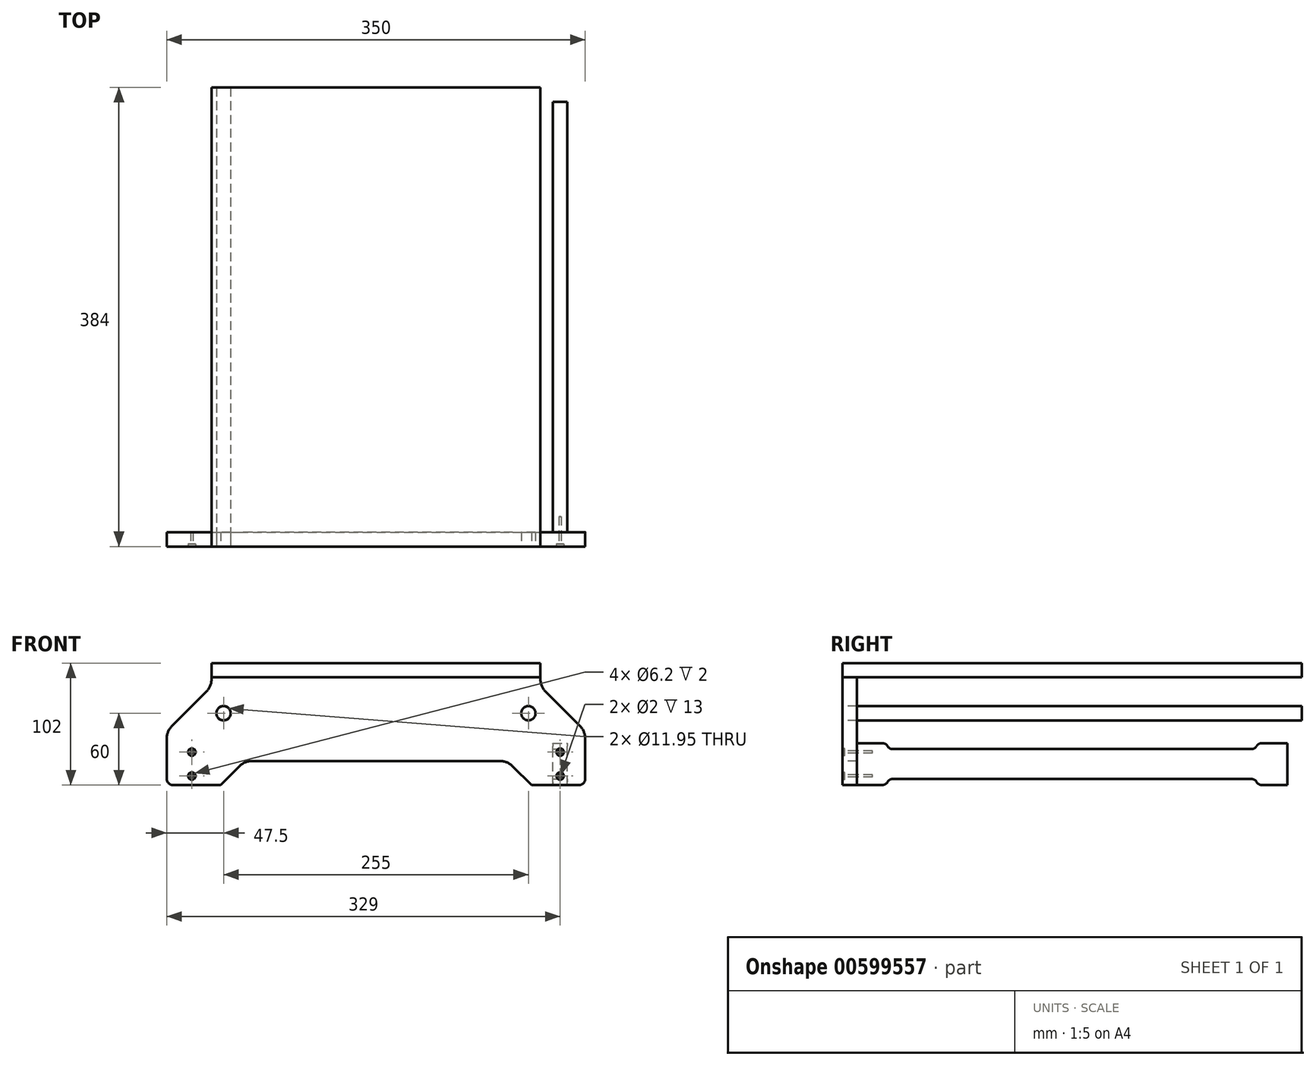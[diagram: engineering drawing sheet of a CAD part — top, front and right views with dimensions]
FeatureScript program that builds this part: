
annotation { "Feature Type Name" : "Feature", "Feature Type Description" : "" }
export const myFeature = defineFeature(function(context is Context, id is Id, definition is map)
    precondition{}
    {
        {
            var Q0;
            Q0=qCreatedBy(makeId("Front.planeOp"),FACE);
            var sketch = newSketch(context, id + "F0", { "sketchPlane" : qUnion([Q0])});
            skLineSegment(sketch, "E0.bottom", {"start": v(-137.5, 0) * mm, "end": v(137.5, 0) * mm});
            skLineSegment(sketch, "E0.top", {"start": v(-175, -90) * mm, "end": v(175, -90) * mm});
            skLineSegment(sketch, "E0.left", {"start": v(-137.5, 0) * mm, "end": v(-175, -90) * mm, "construction": true});
            skLineSegment(sketch, "E0.right", {"start": v(137.5, 0) * mm, "end": v(175, -90) * mm, "construction": true});
            skLineSegment(sketch, "E1", {"start": v(0, 0) * mm, "end": v(0, -90) * mm, "construction": true});
            skLineSegment(sketch, "E2", {"start": v(-175, -90) * mm, "end": v(-175, -45) * mm});
            skLineSegment(sketch, "E3", {"start": v(-175, -45) * mm, "end": v(-137.5, -7.5) * mm});
            skLineSegment(sketch, "E4", {"start": v(-137.5, -7.5) * mm, "end": v(-137.5, 0) * mm});
            skLineSegment(sketch, "E5.MirrorCS", {"start": v(137.5, -7.5) * mm, "end": v(137.5, 0) * mm});
            skLineSegment(sketch, "E6.MirrorCS", {"start": v(175, -45) * mm, "end": v(137.5, -7.5) * mm});
            skLineSegment(sketch, "E7.MirrorCS", {"start": v(175, -90) * mm, "end": v(175, -45) * mm});
            skSolve(sketch);
        }
        {
            var Q0;
            Q0 = qSketchRegion(id + "F0", true);
            extrude(context, id + "F1", {"entities" : qUnion([Q0]), "depth" : 12 * mm, "offsetDistance" : 25 * mm});
        }
        {
            var Q0;
            Q0=makeQuery(id+"F1.opExtrude","CAP_FACE",FACE,{"disambiguationData":[OSD([sQuery(id+"F0.wireOp",EDGE,"E0.bottom"),sQuery(id+"F0.wireOp",EDGE,"E0.top"),sQuery(id+"F0.wireOp",EDGE,"Db9297z0-HztM-tPDV-7j2n-pV0MaHttiBtU"),sQuery(id+"F0.wireOp",EDGE,"ws5DMRmw-QTd8-vzda-Jt7f-uyXxEBe4kZxb"),sQuery(id+"F0.wireOp",EDGE,"MvMPfKiF-jqBY-hYbT-wa1q-WH4llltNyERM"),sQuery(id+"F0.wireOp",EDGE,"yXXL3qDJ-5hGa-htpM-Qtsq-Fe0N1Uz4Vlwm"),sQuery(id+"F0.wireOp",EDGE,"d8d93aa3-85c5-4bdc-b8fc-1645710442690.MirrorCS"),sQuery(id+"F0.wireOp",EDGE,"6c627fb7-9931-441f-9924-80b87e4fa14c0.MirrorCS"),sQuery(id+"F0.wireOp",EDGE,"8b008a98-4391-4453-9b4b-d140ab52eb620.MirrorCS"),sQuery(id+"F0.wireOp",EDGE,"a82d0274-8465-4c41-8a39-7271eadcd95d0.MirrorCS")])],"isStart":false});
            var sketch = newSketch(context, id + "F2", { "sketchPlane" : qUnion([Q0])});
            skCircle(sketch, "E8", {"center": v(-127.5, -30) * mm, "radius": 5.97 * mm});
            skLineSegment(sketch, "E9", {"start": v(0, 0) * mm, "end": v(0, -90) * mm, "construction": true});
            skCircle(sketch, "E10.MirrorC", {"center": v(127.5, -30) * mm, "radius": 5.97 * mm});
            skLineSegment(sketch, "E11", {"start": v(-110, -70) * mm, "end": v(0, -70) * mm});
            skLineSegment(sketch, "E12", {"start": v(-130, -90) * mm, "end": v(0, -90) * mm});
            skLineSegment(sketch, "E13.MirrorCS", {"start": v(110, -70) * mm, "end": v(0, -70) * mm});
            skLineSegment(sketch, "E14.MirrorCS", {"start": v(130, -90) * mm, "end": v(0, -90) * mm});
            skLineSegment(sketch, "E15", {"start": v(-130, -90) * mm, "end": v(-110, -70) * mm});
            skLineSegment(sketch, "E16", {"start": v(110, -70) * mm, "end": v(130, -90) * mm});
            skSolve(sketch);
        }
        {
            var Q0;
            Q0 = qSketchRegion(id + "F2", true);
            extrude(context, id + "F3", {"entities" : qUnion([Q0]), "operationType" : NewBodyOperationType.REMOVE, "oppositeDirection" : true, "depth" : 25 * mm, "offsetDistance" : 25 * mm});
        }
        {
            var Q0;
            Q0=makeQuery(id+"F1.opExtrude","CAP_FACE",FACE,{"disambiguationData":[OSD([sQuery(id+"F0.wireOp",EDGE,"E0.bottom"),sQuery(id+"F0.wireOp",EDGE,"E0.top"),sQuery(id+"F0.wireOp",EDGE,"Db9297z0-HztM-tPDV-7j2n-pV0MaHttiBtU"),sQuery(id+"F0.wireOp",EDGE,"ws5DMRmw-QTd8-vzda-Jt7f-uyXxEBe4kZxb"),sQuery(id+"F0.wireOp",EDGE,"MvMPfKiF-jqBY-hYbT-wa1q-WH4llltNyERM"),sQuery(id+"F0.wireOp",EDGE,"yXXL3qDJ-5hGa-htpM-Qtsq-Fe0N1Uz4Vlwm"),sQuery(id+"F0.wireOp",EDGE,"d8d93aa3-85c5-4bdc-b8fc-1645710442690.MirrorCS"),sQuery(id+"F0.wireOp",EDGE,"6c627fb7-9931-441f-9924-80b87e4fa14c0.MirrorCS"),sQuery(id+"F0.wireOp",EDGE,"8b008a98-4391-4453-9b4b-d140ab52eb620.MirrorCS"),sQuery(id+"F0.wireOp",EDGE,"a82d0274-8465-4c41-8a39-7271eadcd95d0.MirrorCS")])],"isStart":false});
            var sketch = newSketch(context, id + "F4", { "sketchPlane" : qUnion([Q0])});
            skCircle(sketch, "E17", {"center": v(-127.5, -30) * mm, "radius": 6 * mm});
            skSolve(sketch);
        }
        {
            var Q0;
            Q0 = qSketchRegion(id + "F4", true);
            extrude(context, id + "F5", {"entities" : qUnion([Q0]), "oppositeDirection" : true, "depth" : 384 * mm, "offsetDistance" : 25 * mm});
        }
        {
            var Q0;
            Q0=makeQuery(id+"F1.opExtrude","SWEPT_FACE",FACE,{"disambiguationData":[OSD([sQuery(id+"F0.wireOp",EDGE,"E0.bottom")])]});
            var sketch = newSketch(context, id + "F6", { "sketchPlane" : qUnion([Q0])});
            skLineSegment(sketch, "E18.bottom", {"start": v(-137.5, -12) * mm, "end": v(137.5, -12) * mm});
            skLineSegment(sketch, "E18.top", {"start": v(-137.5, 372) * mm, "end": v(137.5, 372) * mm});
            skLineSegment(sketch, "E18.left", {"start": v(-137.5, -12) * mm, "end": v(-137.5, 372) * mm});
            skLineSegment(sketch, "E18.right", {"start": v(137.5, -12) * mm, "end": v(137.5, 372) * mm});
            skSolve(sketch);
        }
        {
            var Q0;
            Q0 = qSketchRegion(id + "F6", true);
            extrude(context, id + "F7", {"entities" : qUnion([Q0]), "depth" : 12 * mm, "offsetDistance" : 25 * mm});
        }
        {
            var Q0;
            Q0=makeQuery(id+"F1.opExtrude","SWEPT_EDGE",EDGE,{"disambiguationData":[OSD([sQuery(id+"F0.wireOp",EDGE,"E0.top"),sQuery(id+"F0.wireOp",EDGE,"FPoq9T64-5Oud-LrSo-KSuJ-r5LH1fMiyHHU")])]});
            var Q1;
            Q1=makeQuery(id+"F3.boolean.opBoolean","COPY",EDGE,{"derivedFrom":makeQuery(id+"F3.opExtrude","SWEPT_EDGE",EDGE,{"disambiguationData":[OSD([sQuery(id+"F0.wireOp",EDGE,"E0.top"),sQuery(id+"F2.wireOp",EDGE,"rhjKnKnN-fBDo-vWaE-Pvd1-9VDqSsNhjCKd"),sQuery(id+"F2.wireOp",EDGE,"E12")])]})});
            var Q2;
            Q2=makeQuery(id+"F3.boolean.opBoolean","COPY",EDGE,{"derivedFrom":makeQuery(id+"F3.opExtrude","SWEPT_EDGE",EDGE,{"disambiguationData":[OSD([sQuery(id+"F0.wireOp",EDGE,"E0.top"),sQuery(id+"F2.wireOp",EDGE,"dd832bca-97e2-4c86-bc4b-3068f898e1980.MirrorCS"),sQuery(id+"F2.wireOp",EDGE,"E14.MirrorCS")])]})});
            var Q3;
            Q3=makeQuery(id+"F1.opExtrude","SWEPT_EDGE",EDGE,{"disambiguationData":[OSD([sQuery(id+"F0.wireOp",EDGE,"E0.top"),sQuery(id+"F0.wireOp",EDGE,"d44177ea-6d28-4c1c-8cf6-3188f45d4e0c0.MirrorCS")])]});
            fillet(context, id + "F8", {"entities" : qUnion([Q0, Q1, Q2, Q3]), "radius" : 5 * mm, "tangentPropagation" : true, "allowEdgeOverflow" : false});
        }
        {
            var Q0;
            Q0=makeQuery(id+"F1.opExtrude","SWEPT_EDGE",EDGE,{"disambiguationData":[OSD([sQuery(id+"F0.wireOp",EDGE,"E3"),sQuery(id+"F0.wireOp",EDGE,"E4")])]});
            var Q1;
            Q1=makeQuery(id+"F1.opExtrude","SWEPT_EDGE",EDGE,{"disambiguationData":[OSD([sQuery(id+"F0.wireOp",EDGE,"E2"),sQuery(id+"F0.wireOp",EDGE,"E3")])]});
            var Q2;
            Q2=makeQuery(id+"F1.opExtrude","SWEPT_EDGE",EDGE,{"disambiguationData":[OSD([sQuery(id+"F0.wireOp",EDGE,"E5.MirrorCS"),sQuery(id+"F0.wireOp",EDGE,"E6.MirrorCS")])]});
            var Q3;
            Q3=makeQuery(id+"F1.opExtrude","SWEPT_EDGE",EDGE,{"disambiguationData":[OSD([sQuery(id+"F0.wireOp",EDGE,"E6.MirrorCS"),sQuery(id+"F0.wireOp",EDGE,"E7.MirrorCS")])]});
            var Q4;
            Q4=makeQuery(id+"F3.boolean.opBoolean","COPY",EDGE,{"derivedFrom":makeQuery(id+"F3.opExtrude","SWEPT_EDGE",EDGE,{"disambiguationData":[OSD([sQuery(id+"F2.wireOp",EDGE,"E11"),sQuery(id+"F2.wireOp",EDGE,"E15")])]})});
            var Q5;
            Q5=makeQuery(id+"F3.boolean.opBoolean","COPY",EDGE,{"derivedFrom":makeQuery(id+"F3.opExtrude","SWEPT_EDGE",EDGE,{"disambiguationData":[OSD([sQuery(id+"F2.wireOp",EDGE,"E13.MirrorCS"),sQuery(id+"F2.wireOp",EDGE,"E16")])]})});
            fillet(context, id + "F9", {"entities" : qUnion([Q0, Q1, Q2, Q3, Q4, Q5]), "radius" : 15 * mm, "tangentPropagation" : true, "allowEdgeOverflow" : false});
        }
        {
            var Q0;
            Q0=makeQuery(id+"F1.opExtrude","CAP_FACE",FACE,{"disambiguationData":[OSD([sQuery(id+"F0.wireOp",EDGE,"E0.bottom"),sQuery(id+"F0.wireOp",EDGE,"E0.top"),sQuery(id+"F0.wireOp",EDGE,"E2"),sQuery(id+"F0.wireOp",EDGE,"E3"),sQuery(id+"F0.wireOp",EDGE,"E4"),sQuery(id+"F0.wireOp",EDGE,"E5.MirrorCS"),sQuery(id+"F0.wireOp",EDGE,"E6.MirrorCS"),sQuery(id+"F0.wireOp",EDGE,"E7.MirrorCS")])],"isStart":true});
            var sketch = newSketch(context, id + "F10", { "sketchPlane" : qUnion([Q0])});
            skLineSegment(sketch, "E19.bottom", {"start": v(-148, -90) * mm, "end": v(-160, -90) * mm});
            skLineSegment(sketch, "E19.top", {"start": v(-148, -55) * mm, "end": v(-160, -55) * mm});
            skLineSegment(sketch, "E19.left", {"start": v(-148, -90) * mm, "end": v(-148, -55) * mm});
            skLineSegment(sketch, "E19.right", {"start": v(-160, -90) * mm, "end": v(-160, -55) * mm});
            skSolve(sketch);
        }
        {
            var Q0;
            Q0 = qSketchRegion(id + "F10", true);
            extrude(context, id + "F11", {"entities" : qUnion([Q0]), "depth" : 360 * mm, "offsetDistance" : 25 * mm});
        }
        {
            var Q0;
            Q0=makeQuery(id+"F1.opExtrude","CAP_FACE",FACE,{"disambiguationData":[OSD([sQuery(id+"F0.wireOp",EDGE,"E0.bottom"),sQuery(id+"F0.wireOp",EDGE,"E0.top"),sQuery(id+"F0.wireOp",EDGE,"E2"),sQuery(id+"F0.wireOp",EDGE,"E3"),sQuery(id+"F0.wireOp",EDGE,"E4"),sQuery(id+"F0.wireOp",EDGE,"E5.MirrorCS"),sQuery(id+"F0.wireOp",EDGE,"E6.MirrorCS"),sQuery(id+"F0.wireOp",EDGE,"E7.MirrorCS")])],"isStart":false});
            var sketch = newSketch(context, id + "F12", { "sketchPlane" : qUnion([Q0])});
            skCircle(sketch, "E20", {"center": v(154, -82.5) * mm, "radius": 1 * mm});
            skCircle(sketch, "E21", {"center": v(154, -62.5) * mm, "radius": 1 * mm});
            skLineSegment(sketch, "E22", {"start": v(154, -62.5) * mm, "end": v(154, -82.5) * mm, "construction": true});
            skCircle(sketch, "E23.MirrorC", {"center": v(-154, -82.5) * mm, "radius": 1 * mm});
            skCircle(sketch, "E24.MirrorC", {"center": v(-154, -62.5) * mm, "radius": 1 * mm});
            skSolve(sketch);
        }
        {
            var Q0;
            Q0 = qSketchRegion(id + "F12", true);
            extrude(context, id + "F13", {"entities" : qUnion([Q0]), "operationType" : NewBodyOperationType.REMOVE, "oppositeDirection" : true, "depth" : 25 * mm, "offsetDistance" : 25 * mm});
        }
        {
            var Q0;
            Q0=makeQuery(id+"F1.opExtrude","CAP_FACE",FACE,{"disambiguationData":[OSD([sQuery(id+"F0.wireOp",EDGE,"E0.bottom"),sQuery(id+"F0.wireOp",EDGE,"E0.top"),sQuery(id+"F0.wireOp",EDGE,"E2"),sQuery(id+"F0.wireOp",EDGE,"E3"),sQuery(id+"F0.wireOp",EDGE,"E4"),sQuery(id+"F0.wireOp",EDGE,"E5.MirrorCS"),sQuery(id+"F0.wireOp",EDGE,"E6.MirrorCS"),sQuery(id+"F0.wireOp",EDGE,"E7.MirrorCS")])],"isStart":false});
            var sketch = newSketch(context, id + "F14", { "sketchPlane" : qUnion([Q0])});
            skCircle(sketch, "E25", {"center": v(154, -62.5) * mm, "radius": 3.1 * mm});
            skCircle(sketch, "E26", {"center": v(154, -82.5) * mm, "radius": 3.1 * mm});
            skCircle(sketch, "E27", {"center": v(-154, -62.5) * mm, "radius": 3.1 * mm});
            skCircle(sketch, "E28", {"center": v(-154, -82.5) * mm, "radius": 3.1 * mm});
            skSolve(sketch);
        }
        {
            var Q0;
            Q0 = qSketchRegion(id + "F14", true);
            extrude(context, id + "F15", {"entities" : qUnion([Q0]), "operationType" : NewBodyOperationType.REMOVE, "oppositeDirection" : true, "depth" : 2 * mm, "offsetDistance" : 25 * mm});
        }
        {
            var Q0;
            Q0=makeQuery(id+"F11.opExtrude","SWEPT_FACE",FACE,{"disambiguationData":[OSD([sQuery(id+"F10.wireOp",EDGE,"E19.right")])]});
            var sketch = newSketch(context, id + "F16", { "sketchPlane" : qUnion([Q0])});
            skLineSegment(sketch, "E29", {"start": v(0, -72.5) * mm, "end": v(360, -72.5) * mm, "construction": true});
            skLineSegment(sketch, "E30.bottom", {"start": v(30, -50) * mm, "end": v(330.01, -50) * mm});
            skLineSegment(sketch, "E30.top", {"start": v(30, -60) * mm, "end": v(330, -60) * mm});
            skArc(sketch, "E31", {"start": v(30, -50) * mm, "mid": v(25, -55) * mm, "end": v(30, -60) * mm});
            skArc(sketch, "E32", {"start": v(330, -60) * mm, "mid": v(335, -55) * mm, "end": v(330.01, -50) * mm});
            skLineSegment(sketch, "E33", {"start": v(30, -55) * mm, "end": v(330, -55) * mm, "construction": true});
            skArc(sketch, "E34.MirrorCS", {"start": v(330, -85) * mm, "mid": v(335, -90) * mm, "end": v(330.01, -95) * mm});
            skLineSegment(sketch, "E35.MirrorCS", {"start": v(30, -95) * mm, "end": v(330.01, -95) * mm});
            skArc(sketch, "E36.MirrorCS", {"start": v(30, -95) * mm, "mid": v(25, -90) * mm, "end": v(30, -85) * mm});
            skLineSegment(sketch, "E37.MirrorCS", {"start": v(30, -85) * mm, "end": v(330, -85) * mm});
            skSolve(sketch);
        }
        {
            var Q0;
            Q0 = qSketchRegion(id + "F16", true);
            extrude(context, id + "F17", {"entities" : qUnion([Q0]), "operationType" : NewBodyOperationType.REMOVE, "oppositeDirection" : true, "depth" : 25 * mm, "offsetDistance" : 25 * mm});
        }
        {
            var Q0;
            Q0=makeQuery(id+"F17.boolean.opBoolean","INTERSECT",EDGE,{"derivedFrom":[makeQuery(id+"F11.opExtrude","SWEPT_FACE",FACE,{"disambiguationData":[OSD([sQuery(id+"F10.wireOp",EDGE,"E19.top")])]}),makeQuery(id+"F17.opExtrude","SWEPT_FACE",FACE,{"disambiguationData":[OSD([sQuery(id+"F16.wireOp",EDGE,"E31")])]})]});
            var Q1;
            Q1=makeQuery(id+"F17.boolean.opBoolean","INTERSECT",EDGE,{"derivedFrom":[makeQuery(id+"F11.opExtrude","SWEPT_FACE",FACE,{"disambiguationData":[OSD([sQuery(id+"F10.wireOp",EDGE,"E19.bottom")])]}),makeQuery(id+"F17.opExtrude","SWEPT_FACE",FACE,{"disambiguationData":[OSD([sQuery(id+"F16.wireOp",EDGE,"E36.MirrorCS")])]})]});
            var Q2;
            Q2=makeQuery(id+"F17.boolean.opBoolean","INTERSECT",EDGE,{"derivedFrom":[makeQuery(id+"F11.opExtrude","SWEPT_FACE",FACE,{"disambiguationData":[OSD([sQuery(id+"F10.wireOp",EDGE,"E19.bottom")])]}),makeQuery(id+"F17.opExtrude","SWEPT_FACE",FACE,{"disambiguationData":[OSD([sQuery(id+"F16.wireOp",EDGE,"E34.MirrorCS")])]})]});
            var Q3;
            Q3=makeQuery(id+"F17.boolean.opBoolean","INTERSECT",EDGE,{"derivedFrom":[makeQuery(id+"F11.opExtrude","SWEPT_FACE",FACE,{"disambiguationData":[OSD([sQuery(id+"F10.wireOp",EDGE,"E19.top")])]}),makeQuery(id+"F17.opExtrude","SWEPT_FACE",FACE,{"disambiguationData":[OSD([sQuery(id+"F16.wireOp",EDGE,"E32")])]})]});
            fillet(context, id + "F18", {"entities" : qUnion([Q0, Q1, Q2, Q3]), "radius" : 5 * mm, "tangentPropagation" : true, "allowEdgeOverflow" : false});
        }
    });
